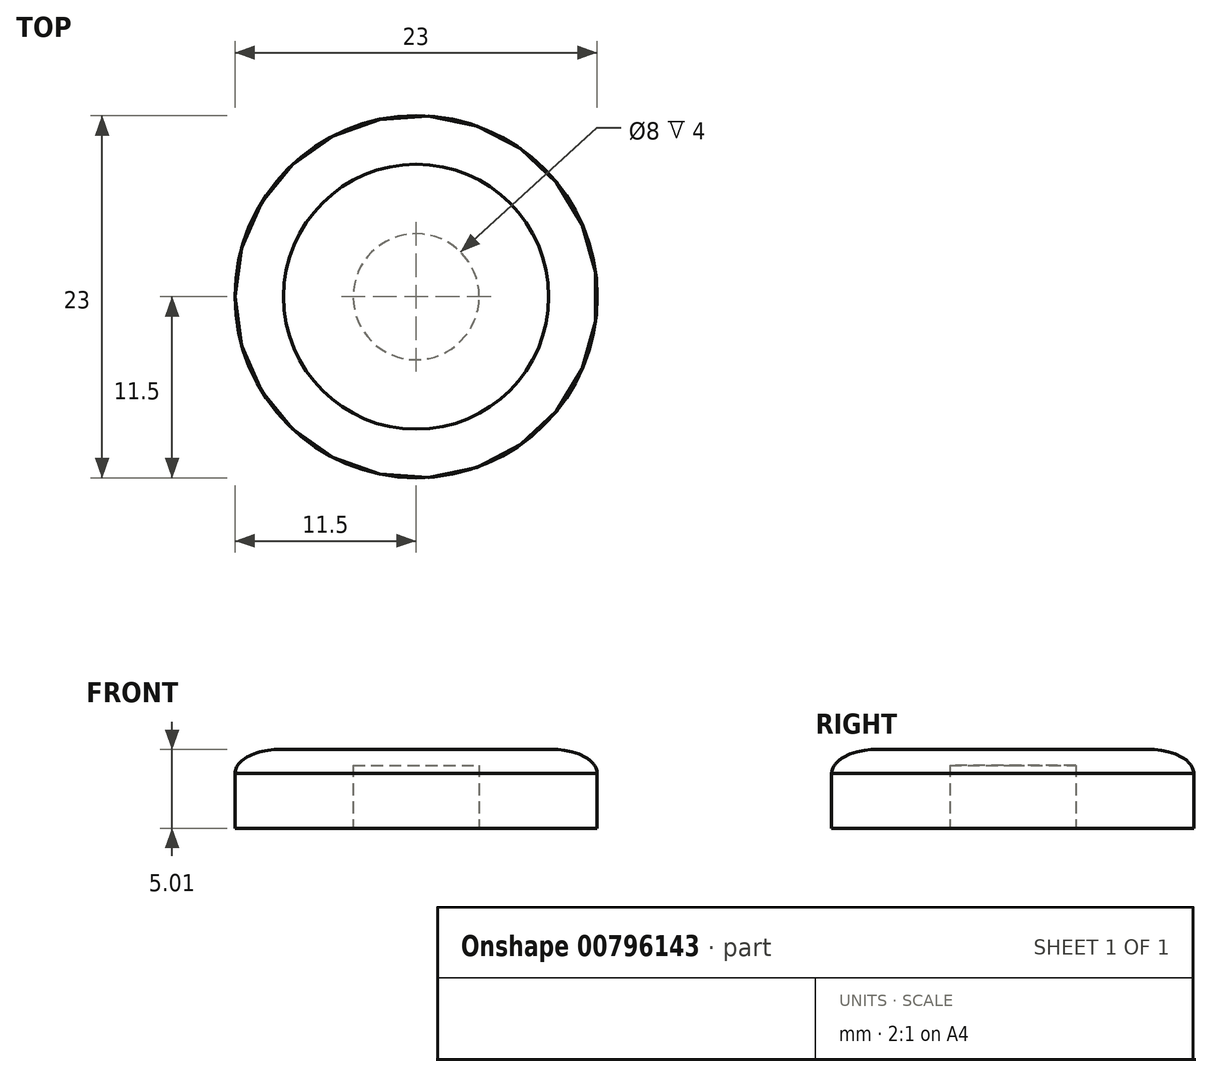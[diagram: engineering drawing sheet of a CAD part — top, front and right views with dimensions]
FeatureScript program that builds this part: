
annotation { "Feature Type Name" : "Feature", "Feature Type Description" : "" }
export const myFeature = defineFeature(function(context is Context, id is Id, definition is map)
    precondition{}
    {
        {
            var Q0;
            Q0=qCreatedBy(makeId("Front.planeOp"),FACE);
            var sketch = newSketch(context, id + "F0", { "sketchPlane" : qUnion([Q0])});
            skLineSegment(sketch, "E0", {"start": v(0, 4) * mm, "end": v(-4, 4) * mm});
            skLineSegment(sketch, "E1", {"start": v(-4, 4) * mm, "end": v(-4, 0) * mm});
            skLineSegment(sketch, "E2", {"start": v(-4, 0) * mm, "end": v(-11.5, 0) * mm});
            skLineSegment(sketch, "E3", {"start": v(-11.5, 0) * mm, "end": v(-11.5, 3.07) * mm});
            skLineSegment(sketch, "E4", {"start": v(-8.42, 5) * mm, "end": v(0, 5) * mm});
            skEllipticalArc(sketch, "E5", {});
            skLineSegment(sketch, "E6", {"start": v(-11.5, 3.07) * mm, "end": v(-11.5, 3.47) * mm});
            skLineSegment(sketch, "E7", {"start": v(0, 6.97) * mm, "end": v(0, -3.16) * mm, "construction": true});
            const initialGuessF0  = {"E5": [-0.00864016810415433, 0.003474369304413344, -1, 0, 0.002859831895845669, 0.0015302607250565411, 4.634579283747395, 0]};
            skSetInitialGuess(sketch, initialGuessF0);
            skSolve(sketch);
        }
        {
            var Q0;
            Q0=sQuery(id+"F0.wireOp",EDGE,"E4");
            var Q1;
            Q1=sQuery(id+"F0.wireOp",EDGE,"E5");
            var Q2;
            Q2=sQuery(id+"F0.wireOp",EDGE,"E6");
            var Q3;
            Q3=sQuery(id+"F0.wireOp",EDGE,"E3");
            var Q4;
            Q4=sQuery(id+"F0.wireOp",EDGE,"E2");
            var Q5;
            Q5=sQuery(id+"F0.wireOp",EDGE,"E1");
            var Q6;
            Q6=sQuery(id+"F0.wireOp",EDGE,"E0");
            var Q7;
            Q7=sQuery(id+"F0.wireOp",EDGE,"E7");
            revolve(context, id + "F1", {"bodyType" : ToolBodyType.SURFACE, "surfaceOperationType" : NewSurfaceOperationType.NEW, "surfaceEntities" : qUnion([Q0, Q1, Q2, Q3, Q4, Q5, Q6]), "axis" : qUnion([Q7]), "revolveType" : RevolveType.FULL});
        }
    });
